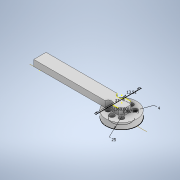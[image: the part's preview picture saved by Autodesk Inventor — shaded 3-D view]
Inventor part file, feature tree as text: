
AUTODESK INVENTOR PART (.ipt)
format: ipt  version: 2022 (Build 260153000, 153)  size: 186,880 bytes
history: native  units: mm
features: sketch x6, extrude x3
ambient origin geometry x8: Origin, YZ Plane, XZ Plane, XY Plane, X Axis, Y Axis, Z Axis, Center Point
bodies: Solid1 (feature_tree)
feature tree (9):
  extrude  "Extrusion1"  Depth=4.0mm
  extrude  "Extrusion2"  Depth=4.0mm
  sketch  "Sketch4"  dims[d9=20.0mm d11=360.0deg d13=5.0mm d14=0.0mm]
  extrude  "Extrusion6"  Depth=5.0mm TaperAngle=0.0deg
  sketch  "Sketch33"  dims[d25=90.0deg]
  sketch  "Sketch34"  dims[d26=70.0mm d27=4.0mm d28=4.0mm d29=4.0mm d30=4.0mm d31=5.0mm d32=0.0mm d50=6.0mm d51=6.0mm d52=6.0mm d53=6.0mm d54=39.25mm d55=0.0mm d105=13.51mm d106=37.0mm d73=0.5mm d74=0.872665mm d75=0.5mm d76=0.872665mm d89=0.5mm d90=0.872665mm d91=0.5mm d92=0.872665mm]
  sketch  "Sketch1"  dims[d0=25.0mm d3=4.0mm]
  sketch  "Sketch2"  dims[d4=40.0mm d6=360.0deg d8=4.0mm]
  sketch  "Sketch8"  dims[d24=10.0mm]
